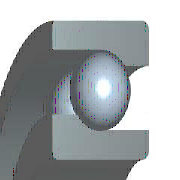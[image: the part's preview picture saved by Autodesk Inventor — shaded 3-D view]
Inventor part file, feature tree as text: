
AUTODESK INVENTOR PART (.ipt)
format: ipt  version: 2019 (Build 230136000, 136)  size: 311,296 bytes
history: native  units: mm (DEFAULTED — no unit token found)
features: sketch x7, other x5, plane x3, fillet x2, pattern_circular x1
ambient origin geometry x8: Origin, YZ Plane, XZ Plane, XY Plane, X Axis, Y Axis, Z Axis, Center Point
bodies: Solid1 (feature_tree)
feature tree (18):
  plane  "WorkPlane1"
  plane  "Work Plane2"
  plane  "WorkPlane2"
  sketch  "Sketch1"  dims[d0=-12.0mm]
  other  "WorkPoint1"
  sketch  "Sketch2"  dims[d1=10.0mm]
  other  "WorkPoint3"
  sketch  "Sketch3"  dims[d2=8.5mm]
  other  "WorkPoint2"
  other  "WorkAxis1"
  sketch  "Sketch7"  dims[d9=6.0mm d10=8.1mm d11=6.9mm d12=360.0deg d13=4.05mm d14=3.45mm d15=360.0deg d16=60.0mm d18=360.0deg d19=0.6mm d20=0.6mm d21=28.5mm d22=24.36mm d23=32.64mm d26=0.0mm d27=0.0mm d28=0.0mm d29=0.0mm d30=0.0mm]
  other  "Work Axis2"
  pattern_circular  "PolarArray1"  Count=2  [1 undecoded]
  fillet  "Fillet1"  Radius=14.0mm
  fillet  "Fillet2"  Radius=12.0mm
  sketch  "Sketch4"  dims[d3=23.5mm d4=20.0mm d5=14.0mm d6=12.0mm]
  sketch  "Sketch5"  dims[d7=360.0deg]
  sketch  "Sketch6"  dims[d8=7.0mm]
note: 1 required parameter value undecoded (feature->parameter linkage not recoverable at this tier; creation-order binding heuristic only, values carry confidence <= 0.55)
